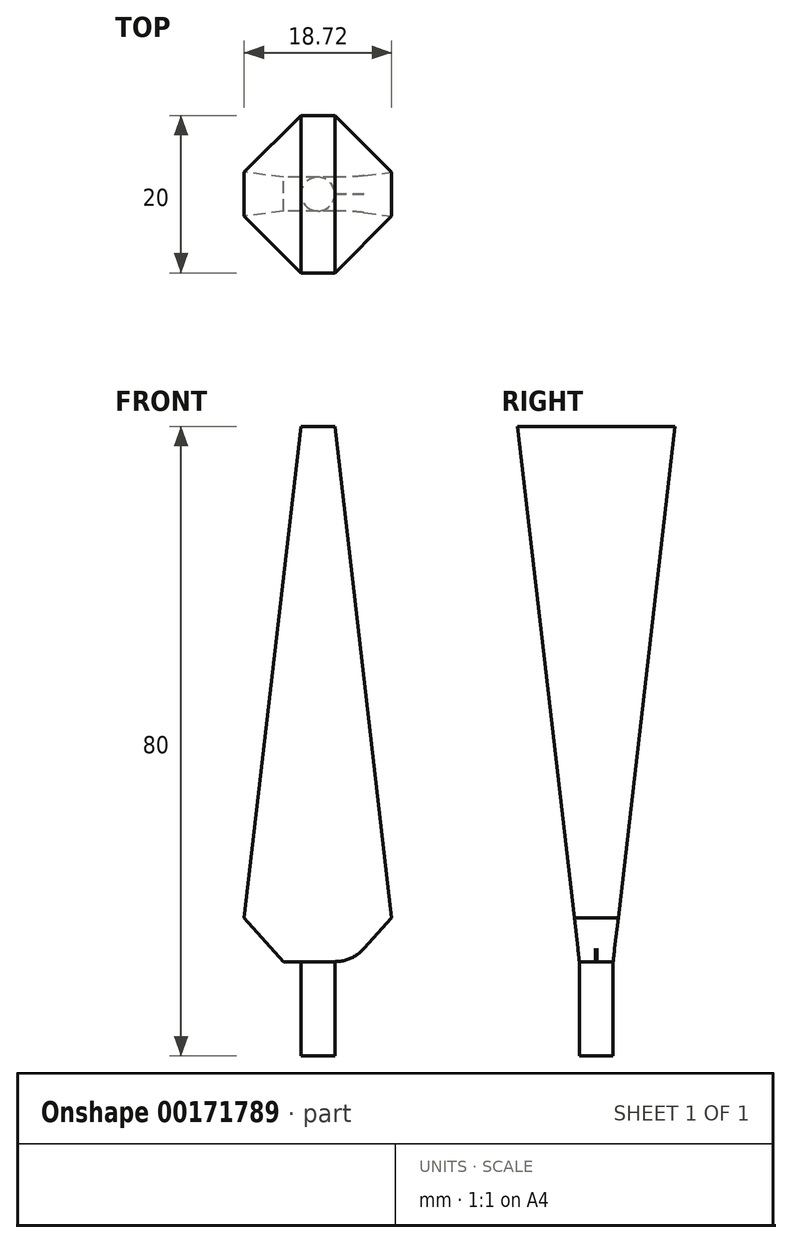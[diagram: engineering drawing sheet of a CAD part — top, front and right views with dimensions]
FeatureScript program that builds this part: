
annotation { "Feature Type Name" : "Feature", "Feature Type Description" : "" }
export const myFeature = defineFeature(function(context is Context, id is Id, definition is map)
    precondition{}
    {
        {
            var Q0;
            Q0=qCreatedBy(makeId("Top.planeOp"),FACE);
            var sketch = newSketch(context, id + "F0", { "sketchPlane" : qUnion([Q0])});
            skCircle(sketch, "E0", {"center": v(0, 0) * mm, "radius": 2.15 * mm});
            skSolve(sketch);
        }
        {
            var Q0;
            Q0 = qSketchRegion(id + "F0", true);
            extrude(context, id + "F1", {"entities" : qUnion([Q0]), "depth" : 12 * mm});
        }
        {
            var Q0;
            Q0=makeQuery(id+"F1.opExtrude","CAP_FACE",FACE,{"disambiguationData":[OSD([sQuery(id+"F0.wireOp",EDGE,"E0")])],"isStart":false});
            var sketch = newSketch(context, id + "F2", { "sketchPlane" : qUnion([Q0])});
            skLineSegment(sketch, "E1.bottom", {"start": v(10, 2.15) * mm, "end": v(-10, 2.15) * mm});
            skLineSegment(sketch, "E1.top", {"start": v(10, -2.15) * mm, "end": v(-10, -2.15) * mm});
            skLineSegment(sketch, "E1.left", {"start": v(10, 2.15) * mm, "end": v(10, -2.15) * mm});
            skLineSegment(sketch, "E1.right", {"start": v(-10, 2.15) * mm, "end": v(-10, -2.15) * mm});
            skPoint(sketch, "E1.middle", {"position": v(0, 0) * mm});
            skSolve(sketch);
        }
        {
            var Q0;
            Q0=qCreatedBy(makeId("Top.planeOp"),FACE);
            cPlane(context, id + "F3", {"entities" : qUnion([Q0]), "cplaneType" : CPlaneType.OFFSET, "offset" : 80 * mm, "width" : 150 * mm, "height" : 150 * mm});
        }
        {
            var Q0;
            Q0=qCreatedBy(id+"F3.planeOp",FACE);
            var sketch = newSketch(context, id + "F4", { "sketchPlane" : qUnion([Q0])});
            skLineSegment(sketch, "E2.bottom", {"start": v(-2.15, 10) * mm, "end": v(2.15, 10) * mm});
            skLineSegment(sketch, "E2.top", {"start": v(-2.15, -10) * mm, "end": v(2.15, -10) * mm});
            skLineSegment(sketch, "E2.left", {"start": v(-2.15, 10) * mm, "end": v(-2.15, -10) * mm});
            skLineSegment(sketch, "E2.right", {"start": v(2.15, 10) * mm, "end": v(2.15, -10) * mm});
            skPoint(sketch, "E2.middle", {"position": v(0, 0) * mm});
            skSolve(sketch);
        }
        {
            var Q1;
            Q1 = qSketchRegion(id + "F2", true);
            var Q2;
            Q2 = qSketchRegion(id + "F4", true);
            loft(context, id + "F5", {"operationType" : NewBodyOperationType.ADD, "sheetProfilesArray" : [{ "sheetProfileEntities" : qUnion([Q1]) }, { "sheetProfileEntities" : qUnion([Q2]) }]});
        }
        {
            var Q0;
            Q0=makeQuery(id+"F5.opLoft","MID_CAP_EDGE",EDGE,{"disambiguationData":[OSD([sQuery(id+"F2.wireOp",EDGE,"E1.bottom"),sQuery(id+"F2.wireOp",EDGE,"E1.top"),sQuery(id+"F2.wireOp",EDGE,"E1.right")])],"capPos":0.0});
            var Q1;
            Q1=makeQuery(id+"F5.opLoft","MID_CAP_EDGE",EDGE,{"disambiguationData":[OSD([sQuery(id+"F2.wireOp",EDGE,"E1.bottom"),sQuery(id+"F2.wireOp",EDGE,"E1.top"),sQuery(id+"F2.wireOp",EDGE,"E1.left")])],"capPos":0.0});
            chamfer(context, id + "F6", {"entities" : qUnion([Q0, Q1]), "width" : 5 * mm, "tangentPropagation" : true});
        }
        {
            var Q0;
            {var subQ0=sQuery(id+"F4.wireOp",EDGE,"E2.right");var subQ2=sQuery(id+"F4.wireOp",EDGE,"E2.top");var subQ3=sQuery(id+"F2.wireOp",EDGE,"E1.left");var subQ4=sQuery(id+"F2.wireOp",EDGE,"E1.top");var subQ5=sQuery(id+"F0.wireOp",EDGE,"E0");var subQ6=sQuery(id+"F4.wireOp",EDGE,"E2.bottom");var subQ7=sQuery(id+"F2.wireOp",EDGE,"E1.bottom");var subQ8=makeQuery(id+"F1.opExtrude","CAP_EDGE",EDGE,{"disambiguationData":[OSD([subQ5])],"isStart":false});var subQ9=makeQuery(id+"F2.imprint","INTERSECT",VERTEX,{"derivedFrom":[subQ8,subQ7]});var subQ11=makeQuery(id+"F5.opLoft","CAP_FACE",FACE,{"disambiguationData":[OSD([makeQuery(id+"F2.imprint","IMPRINT",FACE,{"disambiguationData":[TD([[makeQuery(id+"F2.imprint","IMPRINT",EDGE,{"disambiguationData":[TD([[subQ9,1.0]])],"derivedFrom":subQ8}),1.0]])]})])],"isStart":true});Q0=makeQuery(id+"F6.opChamfer","BLEND_EDGE",EDGE,{"blendedFrom":[makeQuery(id+"F5.opLoft","MID_CAP_EDGE",EDGE,{"disambiguationData":[OSD([subQ7,subQ4,subQ3])],"capPos":0.0}),makeQuery(id+"F5.boolean.opBoolean","SPLIT",FACE,{"disambiguationData":[TD([makeQuery(id+"F5.opLoft","SWEPT_FACE",FACE,{"disambiguationData":[OSD([subQ7,subQ4,subQ3,subQ6,subQ2,subQ0])]})])],"derivedFrom":subQ11})],"blendedInto":[makeQuery(id+"F5.boolean.opBoolean","SPLIT",FACE,{"disambiguationData":[TD([makeQuery(id+"F5.opLoft","SWEPT_FACE",FACE,{"disambiguationData":[OSD([subQ7,subQ4,subQ3,subQ6,subQ2,subQ0])]})])],"derivedFrom":subQ11})]});}
            fillet(context, id + "F7", {"entities" : qUnion([Q0]), "radius" : 5 * mm, "tangentPropagation" : true, "allowEdgeOverflow" : false});
        }
    });
